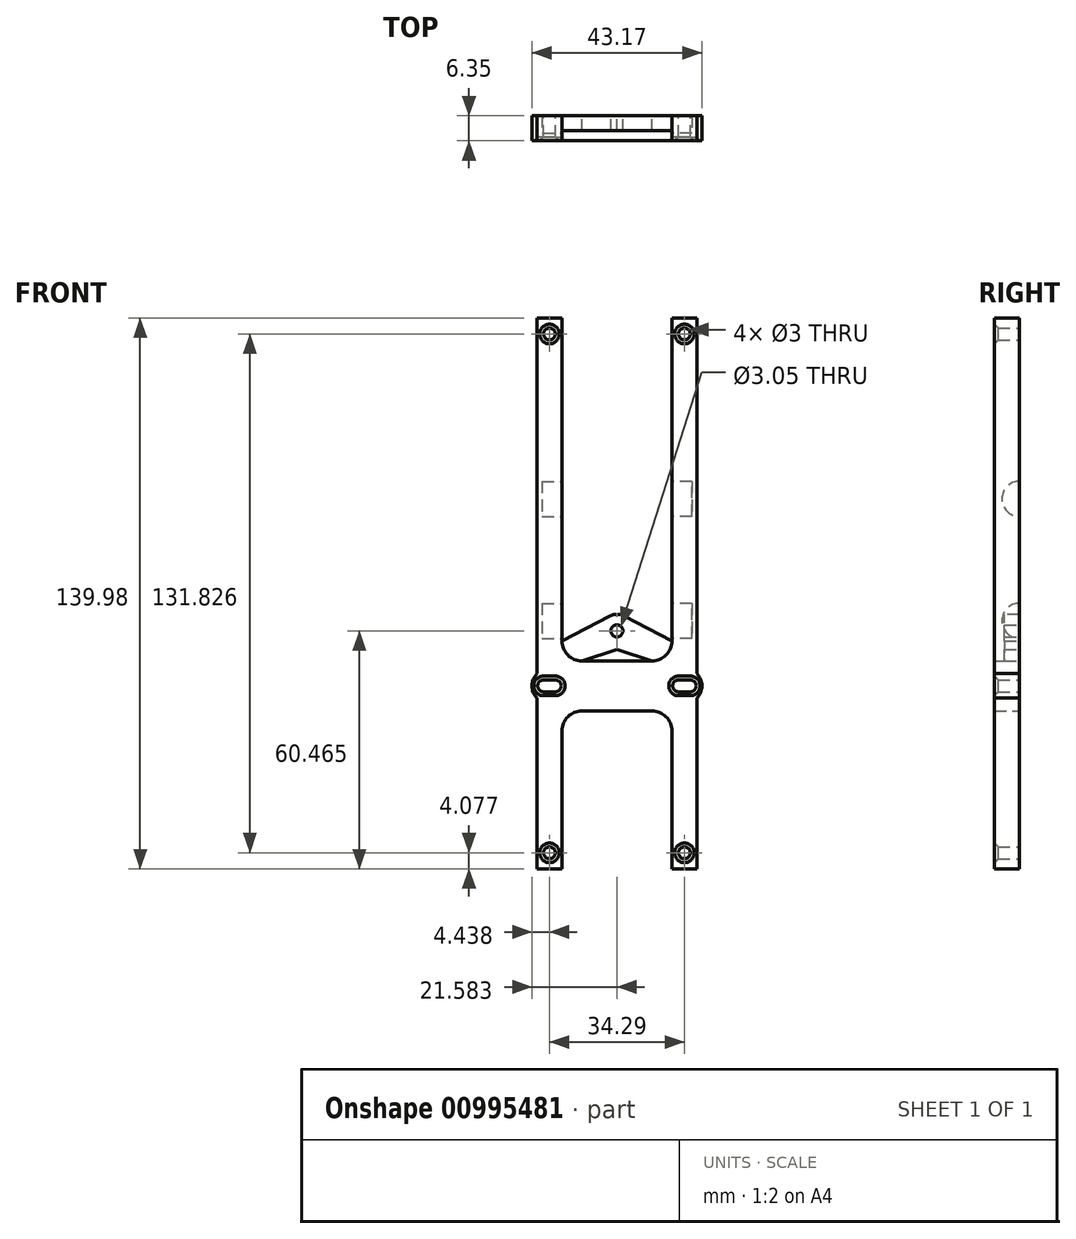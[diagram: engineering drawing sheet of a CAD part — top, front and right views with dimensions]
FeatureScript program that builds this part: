
annotation { "Feature Type Name" : "Feature", "Feature Type Description" : "" }
export const myFeature = defineFeature(function(context is Context, id is Id, definition is map)
    precondition{}
    {
        {
            var Q0;
            Q0=qCreatedBy(makeId("Front.planeOp"),FACE);
            var sketch = newSketch(context, id + "F0", { "sketchPlane" : qUnion([Q0])});
            skLineSegment(sketch, "E0.bottom", {"start": v(-42.44, 143.2) * mm, "end": v(-36.09, 143.2) * mm});
            skLineSegment(sketch, "E0.top", {"start": v(-42.44, 3.23) * mm, "end": v(-36.09, 3.23) * mm});
            skLineSegment(sketch, "E0.left", {"start": v(-42.44, 143.2) * mm, "end": v(-42.44, 52.83) * mm});
            skLineSegment(sketch, "E0.right", {"start": v(-36.09, 143.2) * mm, "end": v(-36.09, 61.15) * mm});
            skCircle(sketch, "E1", {"center": v(-39.26, 7.3) * mm, "radius": 1.5 * mm});
            skCircle(sketch, "E2", {"center": v(-39.26, 139.13) * mm, "radius": 1.5 * mm});
            skLineSegment(sketch, "E3.0", {"start": v(-40.76, 51.22) * mm, "end": v(-37.76, 51.22) * mm});
            skLineSegment(sketch, "E4.0", {"start": v(-40.76, 48.23) * mm, "end": v(-37.76, 48.23) * mm});
            skArc(sketch, "E5", {"start": v(-37.76, 48.23) * mm, "mid": v(-36.26, 49.72) * mm, "end": v(-37.76, 51.22) * mm});
            skArc(sketch, "E6", {"start": v(-40.76, 51.22) * mm, "mid": v(-42.26, 49.72) * mm, "end": v(-40.76, 48.23) * mm});
            skArc(sketch, "E7", {"start": v(-42.44, 52.83) * mm, "mid": v(-43.7, 49.72) * mm, "end": v(-42.44, 46.62) * mm});
            skPoint(sketch, "E7.centerSnap0", {"position": v(-39.26, 51.22) * mm});
            skLineSegment(sketch, "E8.trimOffspring", {"start": v(-42.44, 46.62) * mm, "end": v(-42.44, 3.23) * mm});
            skLineSegment(sketch, "E9.trimOffspring", {"start": v(-36.09, 38.3) * mm, "end": v(-36.09, 3.23) * mm});
            skLineSegment(sketch, "E10.bottom", {"start": v(-8.15, 143.2) * mm, "end": v(-1.8, 143.2) * mm});
            skLineSegment(sketch, "E10.top", {"start": v(-8.15, 3.23) * mm, "end": v(-1.8, 3.23) * mm});
            skLineSegment(sketch, "E10.left", {"start": v(-8.15, 143.2) * mm, "end": v(-8.15, 61.15) * mm});
            skLineSegment(sketch, "E10.right", {"start": v(-1.8, 143.2) * mm, "end": v(-1.8, 52.83) * mm});
            skCircle(sketch, "E11", {"center": v(-4.97, 7.3) * mm, "radius": 1.5 * mm});
            skCircle(sketch, "E12", {"center": v(-4.97, 139.13) * mm, "radius": 1.5 * mm});
            skLineSegment(sketch, "E13.0", {"start": v(-6.47, 51.22) * mm, "end": v(-3.47, 51.22) * mm});
            skLineSegment(sketch, "E14.0", {"start": v(-6.47, 48.23) * mm, "end": v(-3.47, 48.23) * mm});
            skArc(sketch, "E15", {"start": v(-3.47, 48.23) * mm, "mid": v(-1.97, 49.72) * mm, "end": v(-3.47, 51.22) * mm});
            skArc(sketch, "E16", {"start": v(-6.47, 51.22) * mm, "mid": v(-7.97, 49.72) * mm, "end": v(-6.47, 48.23) * mm});
            skPoint(sketch, "E17.centerSnap0", {"position": v(-4.97, 51.22) * mm});
            skLineSegment(sketch, "E18.trimOffspring", {"start": v(-8.15, 38.3) * mm, "end": v(-8.15, 3.23) * mm});
            skLineSegment(sketch, "E19.trimOffspring", {"start": v(-1.8, 46.62) * mm, "end": v(-1.8, 3.23) * mm});
            skArc(sketch, "E20.trimOffspring", {"start": v(-1.8, 46.62) * mm, "mid": v(-0.53, 49.72) * mm, "end": v(-1.8, 52.83) * mm});
            skLineSegment(sketch, "E21.0", {"start": v(-31, 43.37) * mm, "end": v(-13.23, 43.37) * mm});
            skLineSegment(sketch, "E22.0", {"start": v(-31, 56.07) * mm, "end": v(-13.23, 56.07) * mm});
            skArc(sketch, "E23.filletArc", {"start": v(-36.09, 61.15) * mm, "mid": v(-34.6, 57.56) * mm, "end": v(-31, 56.07) * mm});
            skArc(sketch, "E24.filletArc", {"start": v(-13.23, 56.07) * mm, "mid": v(-9.63, 57.56) * mm, "end": v(-8.15, 61.15) * mm});
            skArc(sketch, "E25.filletArc", {"start": v(-8.15, 38.3) * mm, "mid": v(-9.63, 41.89) * mm, "end": v(-13.23, 43.37) * mm});
            skArc(sketch, "E26.filletArc", {"start": v(-31, 43.37) * mm, "mid": v(-34.6, 41.89) * mm, "end": v(-36.09, 38.3) * mm});
            skCircle(sketch, "E27", {"center": v(-22.12, 63.7) * mm, "radius": 1.52 * mm});
            skLineSegment(sketch, "E28", {"start": v(-36.09, 61.15) * mm, "end": v(-22.12, 68.4) * mm});
            skLineSegment(sketch, "E29", {"start": v(-8.15, 61.15) * mm, "end": v(-22.12, 68.4) * mm});
            skLineSegment(sketch, "E30", {"start": v(-13.23, 56.07) * mm, "end": v(-22.12, 59) * mm});
            skLineSegment(sketch, "E31", {"start": v(-31, 56.07) * mm, "end": v(-22.12, 59) * mm});
            skPoint(sketch, "E32.orphan", {"position": v(-22.12, 56.07) * mm});
            skSolve(sketch);
        }
        {
            var Q0;
            Q0=makeQuery(id+"F0.imprint","IMPRINT",FACE,{"disambiguationData":[TD([[makeQuery(id+"F0.imprint","IMPRINT",EDGE,{"derivedFrom":sQuery(id+"F0.wireOp",EDGE,"E0.bottom")}),-1.0]])]});
            extrude(context, id + "F1", {"entities" : qUnion([Q0]), "depth" : 6.35 * mm, "offsetDistance" : 25.4 * mm});
        }
        {
            var Q0;
            Q0=makeQuery(id+"F1.opExtrude","CAP_EDGE",EDGE,{"disambiguationData":[OSD([sQuery(id+"F0.wireOp",EDGE,"E1")])],"isStart":false});
            var Q1;
            Q1=makeQuery(id+"F1.opExtrude","CAP_EDGE",EDGE,{"disambiguationData":[OSD([sQuery(id+"F0.wireOp",EDGE,"E5")])],"isStart":false});
            var Q2;
            Q2=makeQuery(id+"F1.opExtrude","CAP_EDGE",EDGE,{"disambiguationData":[OSD([sQuery(id+"F0.wireOp",EDGE,"E2")])],"isStart":false});
            var Q3;
            Q3=makeQuery(id+"F1.opExtrude","CAP_EDGE",EDGE,{"disambiguationData":[OSD([sQuery(id+"F0.wireOp",EDGE,"E14.0")])],"isStart":false});
            var Q4;
            Q4=makeQuery(id+"F1.opExtrude","CAP_EDGE",EDGE,{"disambiguationData":[OSD([sQuery(id+"F0.wireOp",EDGE,"E11")])],"isStart":false});
            var Q5;
            Q5=makeQuery(id+"F1.opExtrude","CAP_EDGE",EDGE,{"disambiguationData":[OSD([sQuery(id+"F0.wireOp",EDGE,"E12")])],"isStart":false});
            chamfer(context, id + "F2", {"entities" : qUnion([Q0, Q1, Q2, Q3, Q4, Q5]), "width" : 1 * mm, "tangentPropagation" : true});
        }
        {
            var Q0;
            Q0=makeQuery(id+"F0.imprint","IMPRINT",FACE,{"disambiguationData":[TD([[makeQuery(id+"F0.imprint","IMPRINT",EDGE,{"derivedFrom":sQuery(id+"F0.wireOp",EDGE,"E23.filletArc")}),1.0]])]});
            extrude(context, id + "F3", {"entities" : qUnion([Q0]), "operationType" : NewBodyOperationType.ADD, "depth" : 3.8 * mm, "offsetDistance" : 25.4 * mm});
        }
        {
            var Q0;
            Q0=makeQuery(id+"F1.opExtrude","SWEPT_FACE",FACE,{"disambiguationData":[OSD([sQuery(id+"F0.wireOp",EDGE,"E10.left")])]});
            var sketch = newSketch(context, id + "F4", { "sketchPlane" : qUnion([Q0])});
            skLineSegment(sketch, "E33", {"start": v(0, 143.2) * mm, "end": v(0, 97.24) * mm});
            skLineSegment(sketch, "E34", {"start": v(0, 97.24) * mm, "end": v(0, 66.25) * mm});
            skCircle(sketch, "E35", {"center": v(0, 97.24) * mm, "radius": 4.45 * mm});
            skCircle(sketch, "E36", {"center": v(0, 66.25) * mm, "radius": 4.45 * mm});
            skSolve(sketch);
        }
        {
            var Q0;
            {var subQ0=sQuery(id+"F4.wireOp",EDGE,"E34");var subQ1=sQuery(id+"F4.wireOp",EDGE,"E33");var subQ2=makeQuery(id+"F4.imprint","INTERSECT",VERTEX,{"derivedFrom":[subQ1,subQ0]});Q0=makeQuery(id+"F4.imprint","IMPRINT",FACE,{"disambiguationData":[TD([[makeQuery(id+"F4.imprint","IMPRINT",EDGE,{"disambiguationData":[TD([[subQ2,1.0]])],"derivedFrom":subQ1}),1.0]])]});}
            var Q1;
            {var subQ0=sQuery(id+"F4.wireOp",EDGE,"E34");var subQ1=makeQuery(id+"F1.opExtrude","CAP_EDGE",EDGE,{"disambiguationData":[OSD([sQuery(id+"F0.wireOp",EDGE,"E10.left")])],"isStart":true});var subQ2=makeQuery(id+"F4.imprint","INTERSECT",VERTEX,{"derivedFrom":[subQ1,subQ0]});Q1=makeQuery(id+"F4.imprint","IMPRINT",FACE,{"disambiguationData":[TD([[makeQuery(id+"F4.imprint","IMPRINT",EDGE,{"disambiguationData":[TD([[subQ2,1.0]])],"derivedFrom":subQ0}),1.0]])]});}
            extrude(context, id + "F5", {"entities" : qUnion([Q0, Q1]), "operationType" : NewBodyOperationType.REMOVE, "oppositeDirection" : true, "depth" : 5.08 * mm, "offsetDistance" : 25.4 * mm});
        }
        {
            var Q0;
            Q0=makeQuery(id+"F1.opExtrude","SWEPT_FACE",FACE,{"disambiguationData":[OSD([sQuery(id+"F0.wireOp",EDGE,"E0.right")])]});
            var sketch = newSketch(context, id + "F6", { "sketchPlane" : qUnion([Q0])});
            skLineSegment(sketch, "E37", {"start": v(0, 143.2) * mm, "end": v(0, 97.24) * mm});
            skLineSegment(sketch, "E38", {"start": v(0, 97.24) * mm, "end": v(0, 66.25) * mm});
            skCircle(sketch, "E39", {"center": v(0, 97.24) * mm, "radius": 4.45 * mm});
            skCircle(sketch, "E40", {"center": v(0, 66.25) * mm, "radius": 4.45 * mm});
            skSolve(sketch);
        }
        {
            var Q0;
            {var subQ0=sQuery(id+"F6.wireOp",EDGE,"E38");var subQ1=sQuery(id+"F6.wireOp",EDGE,"E37");var subQ2=makeQuery(id+"F6.imprint","INTERSECT",VERTEX,{"derivedFrom":[subQ1,subQ0]});Q0=makeQuery(id+"F6.imprint","IMPRINT",FACE,{"disambiguationData":[TD([[makeQuery(id+"F6.imprint","IMPRINT",EDGE,{"disambiguationData":[TD([[subQ2,1.0]])],"derivedFrom":subQ1}),-1.0]])]});}
            var Q1;
            {var subQ0=sQuery(id+"F6.wireOp",EDGE,"E38");var subQ1=makeQuery(id+"F1.opExtrude","CAP_EDGE",EDGE,{"disambiguationData":[OSD([sQuery(id+"F0.wireOp",EDGE,"E0.right")])],"isStart":true});var subQ2=makeQuery(id+"F6.imprint","INTERSECT",VERTEX,{"derivedFrom":[subQ1,subQ0]});Q1=makeQuery(id+"F6.imprint","IMPRINT",FACE,{"disambiguationData":[TD([[makeQuery(id+"F6.imprint","IMPRINT",EDGE,{"disambiguationData":[TD([[subQ2,1.0]])],"derivedFrom":subQ0}),-1.0]])]});}
            extrude(context, id + "F7", {"entities" : qUnion([Q0, Q1]), "operationType" : NewBodyOperationType.REMOVE, "oppositeDirection" : true, "depth" : 5.08 * mm, "offsetDistance" : 25.4 * mm});
        }
        {
            var Q0;
            Q0=makeQuery(id+"F3.opExtrude","SWEPT_EDGE",EDGE,{"disambiguationData":[OSD([sQuery(id+"F0.wireOp",EDGE,"E28"),sQuery(id+"F0.wireOp",EDGE,"E29")])]});
            fillet(context, id + "F8", {"entities" : qUnion([Q0]), "radius" : 3.8 * mm, "tangentPropagation" : true, "allowEdgeOverflow" : false});
        }
    });
